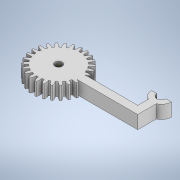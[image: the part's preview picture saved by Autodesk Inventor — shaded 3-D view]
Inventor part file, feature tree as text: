
AUTODESK INVENTOR PART (.ipt)
format: ipt  version: 2022 (Build 260153000, 153)  size: 368,128 bytes
history: native  units: in
note: dims shown in document units (in); Inventor stores cm internally (conversion verified against a paired STEP export)
features: sketch x13, extrude x12, pattern_circular x1
ambient origin geometry x8: Origin, YZ Plane, XZ Plane, XY Plane, X Axis, Y Axis, Z Axis, Center Point
bodies: Solid1 (feature_tree)
feature tree (26):
  extrude  "Extrusion1"  Depth=0.1575in
  pattern_circular  "Circular Pattern1"  Count=26 Angle=360.0deg
  extrude  "Extrusion6"  Depth=0.1969in
  extrude  "Extrusion7"  Depth=1.1811in
  extrude  "Extrusion8"  Depth=0.748in
  extrude  "Extrusion9"  Depth=0.1969in
  extrude  "Extrusion10"  Depth=0.1969in
  extrude  "Extrusion11"  Depth=0.1969in
  extrude  "Extrusion12"  Depth=0.1969in
  extrude  "Extrusion13"  Depth=0.1969in
  extrude  "Extrusion14"  Depth=0.1969in
  extrude  "Extrusion15"  Depth=0.1181in
  sketch  "Sketch18"  dims[d56=0.748in d57=0.1969in]
  extrude  "Extrusion16"  Depth=0.1969in
  sketch  "Sketch1"  dims[d0=0.6299in d1=0.1575in]
  sketch  "Sketch8"  dims[d2=0.0098in]
  sketch  "Sketch9"  dims[d3=0.0098in]
  sketch  "Sketch10"  dims[d4=0.0236in]
  sketch  "Sketch11"  dims[d7=0.0472in]
  sketch  "Sketch12"  dims[d8=0.1772in]
  sketch  "Sketch13"  dims[d10=0.0787in]
  sketch  "Sketch14"  dims[d11=0.1969in d12=0.0in d13=10.2362in d14=360.0deg]
  sketch  "Sketch15"  dims[d49=0.1969in d50=0.1575in]
  sketch  "Sketch16"  dims[d51=0.5438in d52=0.0in d53=1.1811in]
  sketch  "Sketch17"  dims[d54=0.7087in d55=0.748in]
  sketch  "Sketch19"  dims[d58=0.9843in d59=0.0591in d60=0.0591in d61=0.0591in d62=0.3543in d63=0.0591in d64=0.1181in d65=0.1969in d66=0.0197in d67=0.0197in d68=0.0197in d69=0.1969in d70=0.0in d71=1.1811in d72=0.3543in d73=0.1181in d74=0.1181in d75=0.3543in d76=0.1181in d77=0.1969in d78=0.0197in d79=0.1969in d80=0.0197in d81=0.0197in d82=0.1969in d83=0.0in d84=0.1811in d85=0.1969in d86=0.0in d87=1.1811in d88=0.3543in d89=0.1378in d90=0.3937in d91=0.0in d92=0.3937in d93=0.0in d94=1.1811in d95=0.3543in d96=0.1181in d97=0.1378in d98=0.1969in d99=0.1969in d100=0.0in d101=0.1969in d102=0.0in d103=0.1102in d104=0.1969in d105=0.0in d106=0.2874in d107=0.1181in d108=0.0in d109=0.2953in d110=0.1969in d111=0.0in]
